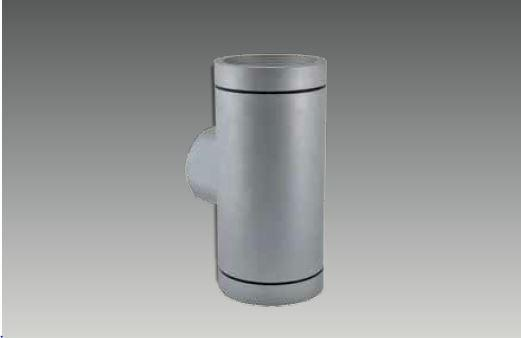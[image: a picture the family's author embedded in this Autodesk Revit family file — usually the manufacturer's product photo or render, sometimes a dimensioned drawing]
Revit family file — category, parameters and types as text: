
# Revit family: B 0315 HDC
name_source: partatom
category: Lighting Fixtures
revit_build: Autodesk Revit 2016 (Build: 20150714_1515(x64)
units: mm (PartAtom-declared; Revit-internal decimal feet)

## family parameters
Always vertical = Yes
Cut with Voids When Loaded = No
Host = Wall
Light Source = Yes
OmniClass Number = 23.80.70.00
OmniClass Title = Lighting
Part Type = Normal
Room Calculation Point = No
Round Connector Dimension = Use Diameter
Shared = No

## types (1)
- BHDC.315.13.27
    Color Filter = 16777215
    Dimming Lamp Color Temperature Shift = <None>
    Emit Shape Visible in Rendering = Yes
    Emit from Circle Diameter = 115 mm  [stored 0.377297 ft]
    Light Source Symbol Size = 610 mm
    Manufacturer = ARLIGHT
    Type Image = B 0315 HDC.JPG
    Wattage Comments = 12,5

note: [stored X ft] marks values corroborated as IEEE doubles in the binary element streams (Revit-internal decimal feet)

## geometry (parser evidence)
native form markers: Sweep x4
no freeform markers — native parametric forms only
